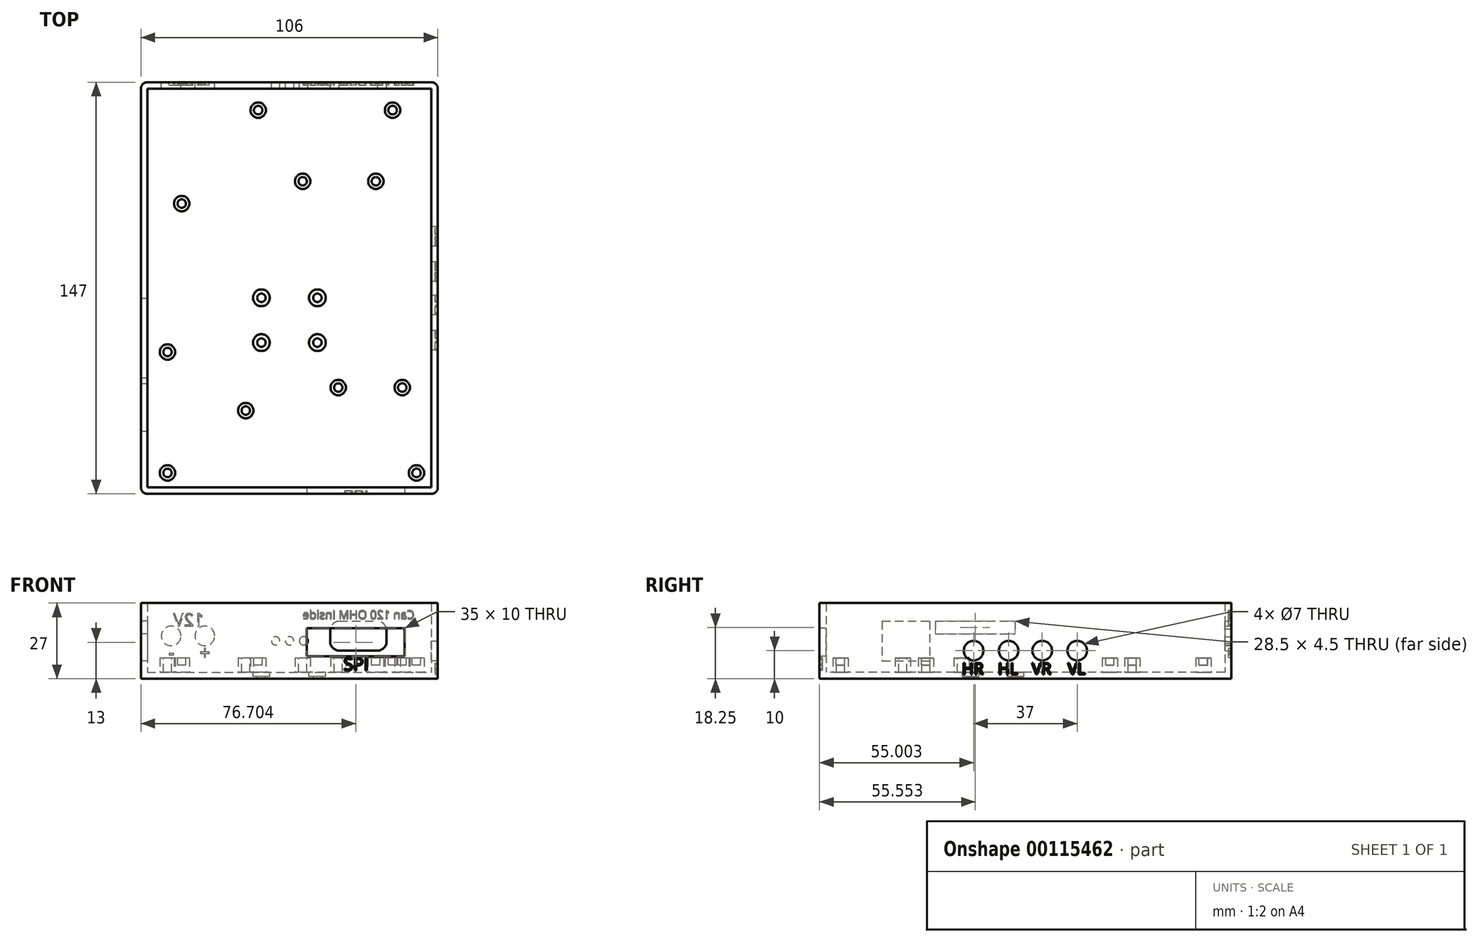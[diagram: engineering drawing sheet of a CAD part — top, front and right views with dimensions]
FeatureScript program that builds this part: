
annotation { "Feature Type Name" : "Feature", "Feature Type Description" : "" }
export const myFeature = defineFeature(function(context is Context, id is Id, definition is map)
    precondition{}
    {
        {
            var Q0;
            Q0=qCreatedBy(makeId("Top.planeOp"),FACE);
            var sketch = newSketch(context, id + "F0", { "sketchPlane" : qUnion([Q0])});
            skLineSegment(sketch, "E0.bottom", {"start": v(-44.59, 115.02) * mm, "end": v(61.41, 115.02) * mm});
            skLineSegment(sketch, "E0.top", {"start": v(-44.59, -31.98) * mm, "end": v(61.41, -31.98) * mm});
            skLineSegment(sketch, "E0.left", {"start": v(-44.59, 115.02) * mm, "end": v(-44.59, -31.98) * mm});
            skLineSegment(sketch, "E0.right", {"start": v(61.41, 115.02) * mm, "end": v(61.41, -31.98) * mm});
            skSolve(sketch);
        }
        {
            var Q0;
            Q0 = qSketchRegion(id + "F0", true);
            extrude(context, id + "F1", {"entities" : qUnion([Q0]), "depth" : 27 * mm});
        }
        {
            var Q0;
            Q0=makeQuery(id+"F1.opExtrude","CAP_FACE",FACE,{"disambiguationData":[OSD([sQuery(id+"F0.wireOp",EDGE,"E0.bottom"),sQuery(id+"F0.wireOp",EDGE,"E0.top"),sQuery(id+"F0.wireOp",EDGE,"E0.left"),sQuery(id+"F0.wireOp",EDGE,"E0.right")])],"isStart":false});
            shell(context, id + "F2", {"entities" : qUnion([Q0]), "thickness" : 2.3 * mm});
        }
        {
            var Q0;
            Q0=makeQuery(id+"F1.opExtrude","SWEPT_FACE",FACE,{"disambiguationData":[OSD([sQuery(id+"F0.wireOp",EDGE,"E0.left")])]});
            var sketch = newSketch(context, id + "F3", { "sketchPlane" : qUnion([Q0])});
            skLineSegment(sketch, "E1", {"start": v(-115.02, 27) * mm, "end": v(-115.02, 0) * mm});
            skLineSegment(sketch, "E2", {"start": v(-115.02, 27) * mm, "end": v(-115.02, 13.5) * mm});
            skLineSegment(sketch, "E3", {"start": v(29.68, 11.5) * mm, "end": v(29.68, 27) * mm});
            skPoint(sketch, "E4.orphan", {"position": v(31.98, 13.5) * mm});
            skPoint(sketch, "E5.left.end.orphan", {"position": v(9.68, 20.5) * mm});
            skLineSegment(sketch, "E6.bottom", {"start": v(9.68, 20.5) * mm, "end": v(-7.32, 20.5) * mm});
            skLineSegment(sketch, "E6.top", {"start": v(9.68, 6.3) * mm, "end": v(-7.32, 6.3) * mm});
            skLineSegment(sketch, "E6.left", {"start": v(9.68, 20.5) * mm, "end": v(9.68, 6.3) * mm});
            skLineSegment(sketch, "E6.right", {"start": v(-7.32, 20.5) * mm, "end": v(-7.32, 6.3) * mm});
            skLineSegment(sketch, "E7", {"start": v(-7.32, 20.5) * mm, "end": v(-9.32, 20.5) * mm});
            skLineSegment(sketch, "E8.bottom", {"start": v(-9.32, 20.5) * mm, "end": v(-37.82, 20.5) * mm});
            skLineSegment(sketch, "E8.top", {"start": v(-9.32, 16) * mm, "end": v(-37.82, 16) * mm});
            skLineSegment(sketch, "E8.left", {"start": v(-9.32, 20.5) * mm, "end": v(-9.32, 16) * mm});
            skLineSegment(sketch, "E8.right", {"start": v(-37.82, 20.5) * mm, "end": v(-37.82, 16) * mm});
            skLineSegment(sketch, "E9", {"start": v(-41.52, 27) * mm, "end": v(-41.52, 0) * mm, "construction": true});
            skLineSegment(sketch, "E10", {"start": v(-115.02, 13.5) * mm, "end": v(31.98, 13.5) * mm, "construction": true});
            skSolve(sketch);
        }
        {
            var Q0;
            Q0 = qSketchRegion(id + "F3", true);
            extrude(context, id + "F4", {"entities" : qUnion([Q0]), "operationType" : NewBodyOperationType.REMOVE, "endBound" : BoundingType.UP_TO_NEXT, "oppositeDirection" : true, "depth" : 25 * mm});
        }
        {
            var Q0;
            Q0=makeQuery(id+"F1.opExtrude","SWEPT_EDGE",EDGE,{"disambiguationData":[OSD([sQuery(id+"F0.wireOp",EDGE,"E0.top"),sQuery(id+"F0.wireOp",EDGE,"E0.left")])]});
            var Q1;
            Q1=makeQuery(id+"F1.opExtrude","SWEPT_EDGE",EDGE,{"disambiguationData":[OSD([sQuery(id+"F0.wireOp",EDGE,"E0.top"),sQuery(id+"F0.wireOp",EDGE,"E0.right")])]});
            var Q2;
            Q2=makeQuery(id+"F1.opExtrude","SWEPT_EDGE",EDGE,{"disambiguationData":[OSD([sQuery(id+"F0.wireOp",EDGE,"E0.bottom"),sQuery(id+"F0.wireOp",EDGE,"E0.right")])]});
            var Q3;
            Q3=makeQuery(id+"F1.opExtrude","SWEPT_EDGE",EDGE,{"disambiguationData":[OSD([sQuery(id+"F0.wireOp",EDGE,"E0.bottom"),sQuery(id+"F0.wireOp",EDGE,"E0.left")])]});
            fillet(context, id + "F5", {"entities" : qUnion([Q0, Q1, Q2, Q3]), "radius" : 2.3 * mm, "tangentPropagation" : true, "allowEdgeOverflow" : false});
        }
        {
            var Q0;
            Q0=makeQuery(id+"F1.opExtrude","SWEPT_FACE",FACE,{"disambiguationData":[OSD([sQuery(id+"F0.wireOp",EDGE,"E0.top")])]});
            var sketch = newSketch(context, id + "F6", { "sketchPlane" : qUnion([Q0])});
            skLineSegment(sketch, "E11", {"start": v(-42.29, 8) * mm, "end": v(59.11, 8) * mm, "construction": true});
            skLineSegment(sketch, "E12.top", {"start": v(23.11, 8) * mm, "end": v(58.16, 8) * mm});
            skPoint(sketch, "E13.end.orphan", {"position": v(12.91, 8) * mm});
            skLineSegment(sketch, "E14", {"start": v(12.91, 8) * mm, "end": v(38.58, 8) * mm});
            skLineSegment(sketch, "E15.bottom", {"start": v(14.61, 8) * mm, "end": v(49.61, 8) * mm});
            skLineSegment(sketch, "E15.top", {"start": v(14.61, 18) * mm, "end": v(49.61, 18) * mm});
            skLineSegment(sketch, "E15.left", {"start": v(14.61, 8) * mm, "end": v(14.61, 18) * mm});
            skLineSegment(sketch, "E15.right", {"start": v(49.61, 8) * mm, "end": v(49.61, 18) * mm});
            skLineSegment(sketch, "E16", {"start": v(8.41, 27) * mm, "end": v(8.41, 0) * mm, "construction": true});
            skLineSegment(sketch, "E17", {"start": v(-42.29, 13.5) * mm, "end": v(59.11, 13.5) * mm, "construction": true});
            skSolve(sketch);
        }
        {
            var Q0;
            Q0 = qSketchRegion(id + "F6", true);
            extrude(context, id + "F7", {"entities" : qUnion([Q0]), "operationType" : NewBodyOperationType.REMOVE, "endBound" : BoundingType.UP_TO_NEXT, "oppositeDirection" : true, "depth" : 25 * mm});
        }
        {
            var Q0;
            Q0=makeQuery(id+"F1.opExtrude","SWEPT_FACE",FACE,{"disambiguationData":[OSD([sQuery(id+"F0.wireOp",EDGE,"E0.right")])]});
            var sketch = newSketch(context, id + "F8", { "sketchPlane" : qUnion([Q0])});
            skLineSegment(sketch, "E18", {"start": v(19.52, 10) * mm, "end": v(26.52, 10) * mm});
            skCircle(sketch, "E19", {"center": v(23.02, 10) * mm, "radius": 3.5 * mm});
            skCircle(sketch, "E20", {"center": v(35.52, 10) * mm, "radius": 3.5 * mm});
            skCircle(sketch, "E21", {"center": v(47.52, 10) * mm, "radius": 3.5 * mm});
            skCircle(sketch, "E22", {"center": v(60.02, 10) * mm, "radius": 3.5 * mm});
            skLineSegment(sketch, "E23.trimOffspring", {"start": v(32.02, 10) * mm, "end": v(39.02, 10) * mm});
            skLineSegment(sketch, "E24.trimOffspring", {"start": v(44.02, 10) * mm, "end": v(51.02, 10) * mm});
            skPoint(sketch, "E25.orphan", {"position": v(41.52, 27) * mm});
            skLineSegment(sketch, "E26.trimOffspring", {"start": v(56.52, 10) * mm, "end": v(63.52, 10) * mm});
            skLineSegment(sketch, "E27", {"start": v(41.52, 27) * mm, "end": v(41.52, 0) * mm});
            skLineSegment(sketch, "E28", {"start": v(35.52, 10) * mm, "end": v(-29.68, 10) * mm});
            skLineSegment(sketch, "E29", {"start": v(-29.68, 10) * mm, "end": v(112.72, 10) * mm});
            skSolve(sketch);
        }
        {
            var Q0;
            Q0 = qSketchRegion(id + "F8", true);
            extrude(context, id + "F9", {"entities" : qUnion([Q0]), "operationType" : NewBodyOperationType.REMOVE, "endBound" : BoundingType.UP_TO_NEXT, "oppositeDirection" : true, "depth" : 25 * mm});
        }
        {
            var Q0;
            Q0=makeQuery(id+"F1.opExtrude","SWEPT_FACE",FACE,{"disambiguationData":[OSD([sQuery(id+"F0.wireOp",EDGE,"E0.bottom")])]});
            var sketch = newSketch(context, id + "F10", { "sketchPlane" : qUnion([Q0])});
            skLineSegment(sketch, "E30", {"start": v(-39.9, 10) * mm, "end": v(-26.2, 10) * mm});
            skLineSegment(sketch, "E31", {"start": v(-26.2, 20.5) * mm, "end": v(-39.9, 20.5) * mm});
            skArc(sketch, "E32.trimOffspring", {"start": v(-22.97, 17.81) * mm, "mid": v(-24.12, 19.72) * mm, "end": v(-26.2, 20.5) * mm});
            skArc(sketch, "E33.trimOffspring", {"start": v(-26.2, 10) * mm, "mid": v(-24.13, 10.8) * mm, "end": v(-23, 12.71) * mm});
            skArc(sketch, "E34.trimOffspring", {"start": v(-43.12, 12.7) * mm, "mid": v(-41.98, 10.8) * mm, "end": v(-39.9, 10) * mm});
            skLineSegment(sketch, "E35", {"start": v(-43.12, 12.7) * mm, "end": v(-43.12, 17.8) * mm});
            skPoint(sketch, "E36.center.orphan", {"position": v(-40.53, 15.25) * mm});
            skCircle(sketch, "E37", {"center": v(21.79, 15.25) * mm, "radius": 3.5 * mm});
            skCircle(sketch, "E38", {"center": v(33.79, 15.25) * mm, "radius": 3.5 * mm});
            skPoint(sketch, "E39", {"position": v(42.29, 13.5) * mm});
            skPoint(sketch, "E40.start.orphan", {"position": v(-59.11, 7) * mm});
            skLineSegment(sketch, "E41", {"start": v(-22.97, 17.81) * mm, "end": v(-23, 12.71) * mm});
            skArc(sketch, "E42.trimOffspring", {"start": v(-39.9, 20.5) * mm, "mid": v(-41.97, 19.7) * mm, "end": v(-43.12, 17.8) * mm});
            skPoint(sketch, "E43.center.orphan", {"position": v(-39.9, 12.3) * mm});
            skPoint(sketch, "E44.center.orphan", {"position": v(-39.9, 8.6) * mm});
            skPoint(sketch, "E45.orphan", {"position": v(42.29, 20.72) * mm});
            skPoint(sketch, "E46.start.orphan", {"position": v(-59.11, 20.72) * mm});
            skLineSegment(sketch, "E47", {"start": v(-59.11, 13.5) * mm, "end": v(42.29, 13.5) * mm, "construction": true});
            skCircle(sketch, "E48", {"center": v(-13.5, 13.5) * mm, "radius": 1.5 * mm});
            skCircle(sketch, "E49", {"center": v(-8.5, 13.5) * mm, "radius": 1.5 * mm});
            skCircle(sketch, "E50", {"center": v(-3.5, 13.5) * mm, "radius": 1.5 * mm});
            skLineSegment(sketch, "E51", {"start": v(-8.41, 27) * mm, "end": v(-8.41, 0) * mm, "construction": true});
            skLineSegment(sketch, "E52", {"start": v(-43.12, 15.25) * mm, "end": v(-22.98, 15.3) * mm, "construction": true});
            skLineSegment(sketch, "E53", {"start": v(-33.05, 20.5) * mm, "end": v(-33.02, 10) * mm, "construction": true});
            skSolve(sketch);
        }
        {
            var Q0;
            Q0 = qSketchRegion(id + "F10", true);
            extrude(context, id + "F11", {"entities" : qUnion([Q0]), "operationType" : NewBodyOperationType.REMOVE, "endBound" : BoundingType.UP_TO_NEXT, "oppositeDirection" : true, "depth" : 25 * mm});
        }
        {
            var Q0;
            Q0=makeQuery(id+"F1.opExtrude","SWEPT_FACE",FACE,{"disambiguationData":[OSD([sQuery(id+"F0.wireOp",EDGE,"E0.right")])]});
            var sketch = newSketch(context, id + "F12", { "sketchPlane" : qUnion([Q0])});
            skText(sketch, "E54", { "text": "HR", "fontName": "OpenSans-Regular.ttf"});
            skText(sketch, "E55", { "text": "HL", "fontName": "OpenSans-Regular.ttf"});
            skText(sketch, "E56", { "text": "VR", "fontName": "OpenSans-Regular.ttf"});
            skText(sketch, "E57", { "text": "VL", "fontName": "OpenSans-Regular.ttf"});
            skLineSegment(sketch, "E58", {"start": v(22.84, 5.63) * mm, "end": v(22.84, 9.12) * mm, "construction": true});
            const initialGuessF12  = {"E54": [0.01884, 0.00153, 1, 0, 0.0041], "E55": [0.03172, 0.00153, 1, 0, 0.0041], "E56": [0.04382, 0.00153, 1, 0, 0.0041], "E57": [0.05666, 0.00153, 1, 0, 0.0041]};
            skSetInitialGuess(sketch, initialGuessF12);
            skSolve(sketch);
        }
        {
            var Q0;
            Q0 = qSketchRegion(id + "F12", true);
            extrude(context, id + "F13", {"entities" : qUnion([Q0]), "operationType" : NewBodyOperationType.REMOVE, "oppositeDirection" : true, "depth" : 1 * mm});
        }
        {
            var Q0;
            Q0=makeQuery(id+"F1.opExtrude","SWEPT_FACE",FACE,{"disambiguationData":[OSD([sQuery(id+"F0.wireOp",EDGE,"E0.top")])]});
            var sketch = newSketch(context, id + "F14", { "sketchPlane" : qUnion([Q0])});
            skText(sketch, "E59", { "text": "SPI", "fontName": "OpenSans-Regular.ttf"});
            skPoint(sketch, "E60", {"position": v(32.11, 8) * mm});
            skLineSegment(sketch, "E61", {"start": v(32.11, 7.44) * mm, "end": v(32.11, 10.56) * mm, "construction": true});
            const initialGuessF14  = {"E59": [0.02775, 0.00294, 1, 0, 0.0045]};
            skSetInitialGuess(sketch, initialGuessF14);
            skSolve(sketch);
        }
        {
            var Q0;
            Q0 = qSketchRegion(id + "F14", true);
            extrude(context, id + "F15", {"entities" : qUnion([Q0]), "operationType" : NewBodyOperationType.REMOVE, "oppositeDirection" : true, "depth" : 1 * mm});
        }
        {
            var Q0;
            Q0=makeQuery(id+"F1.opExtrude","SWEPT_FACE",FACE,{"disambiguationData":[OSD([sQuery(id+"F0.wireOp",EDGE,"E0.bottom")])]});
            var sketch = newSketch(context, id + "F16", { "sketchPlane" : qUnion([Q0])});
            skText(sketch, "E62", { "text": "Can 120 OHM Inside", "fontName": "OpenSans-Regular.ttf"});
            skText(sketch, "E63", { "text": "+", "fontName": "OpenSans-Regular.ttf"});
            skText(sketch, "E64", { "text": "-", "fontName": "OpenSans-Regular.ttf"});
            skText(sketch, "E65", { "text": "12V", "fontName": "OpenSans-Regular.ttf"});
            skPoint(sketch, "E66", {"position": v(-33.05, 20.5) * mm});
            skLineSegment(sketch, "E67", {"start": v(-33.05, 24.32) * mm, "end": v(-33.05, 16.73) * mm, "construction": true});
            const initialGuessF16  = {"E62": [-0.05305, 0.0213, 1, 0, 0.00302], "E63": [0.01979, 0.00683, 1, 0, 0.00492], "E64": [0.03263, 0.00695, 1, 0, 0.0048], "E65": [0.02215, 0.01873, 1, 0, 0.0045]};
            skSetInitialGuess(sketch, initialGuessF16);
            skSolve(sketch);
        }
        {
            var Q0;
            Q0 = qSketchRegion(id + "F16", true);
            extrude(context, id + "F17", {"entities" : qUnion([Q0]), "operationType" : NewBodyOperationType.REMOVE, "oppositeDirection" : true, "depth" : 1 * mm});
        }
        {
            var Q0;
            Q0 = qSketchRegion(id + "F16", true);
            extrude(context, id + "F18", {"entities" : qUnion([Q0]), "operationType" : NewBodyOperationType.REMOVE, "oppositeDirection" : true, "depth" : 1 * mm});
        }
        {
            var Q0;
            Q0=makeQuery(id+"F2.opShell","OFFSET_FACE",FACE,{"disambiguationData":[OSD([sQuery(id+"F0.wireOp",EDGE,"E0.bottom"),sQuery(id+"F0.wireOp",EDGE,"E0.top"),sQuery(id+"F0.wireOp",EDGE,"E0.left"),sQuery(id+"F0.wireOp",EDGE,"E0.right")])]});
            var sketch = newSketch(context, id + "F19", { "sketchPlane" : qUnion([Q0])});
            skPoint(sketch, "E68.trimOffspring.end.orphan", {"position": v(59.11, -22.18) * mm});
            skPoint(sketch, "E69.start.orphan", {"position": v(-42.29, -22.18) * mm});
            skPoint(sketch, "E70.orphan", {"position": v(60.61, 112.72) * mm});
            skPoint(sketch, "E71.orphan", {"position": v(59.11, 103.22) * mm});
            skPoint(sketch, "E72.center.orphan", {"position": v(-43.79, -22.18) * mm});
            skSolve(sketch);
        }
        {
            var Q0;
            Q0=makeQuery(id+"F2.opShell","OFFSET_FACE",FACE,{"disambiguationData":[OSD([sQuery(id+"F0.wireOp",EDGE,"E0.bottom"),sQuery(id+"F0.wireOp",EDGE,"E0.top"),sQuery(id+"F0.wireOp",EDGE,"E0.left"),sQuery(id+"F0.wireOp",EDGE,"E0.right")])]});
            var sketch = newSketch(context, id + "F20", { "sketchPlane" : qUnion([Q0])});
            skCircle(sketch, "E73", {"center": v(-1.59, 38.02) * mm, "radius": 3 * mm});
            skCircle(sketch, "E74", {"center": v(18.41, 38.02) * mm, "radius": 3 * mm});
            skCircle(sketch, "E75", {"center": v(-1.59, 22.02) * mm, "radius": 3 * mm});
            skCircle(sketch, "E76", {"center": v(18.41, 22.02) * mm, "radius": 3 * mm});
            skCircle(sketch, "E77", {"center": v(-1.59, 22.02) * mm, "radius": 1.5 * mm});
            skCircle(sketch, "E78", {"center": v(-1.59, 38.02) * mm, "radius": 1.5 * mm});
            skCircle(sketch, "E79", {"center": v(18.41, 38.02) * mm, "radius": 1.5 * mm});
            skCircle(sketch, "E80", {"center": v(18.41, 22.02) * mm, "radius": 1.5 * mm});
            skLineSegment(sketch, "E81", {"start": v(-1.59, 38.02) * mm, "end": v(18.41, 38.02) * mm});
            skLineSegment(sketch, "E82", {"start": v(18.41, 22.02) * mm, "end": v(-1.59, 22.02) * mm, "construction": true});
            skLineSegment(sketch, "E83", {"start": v(-1.59, 38.02) * mm, "end": v(18.41, 38.02) * mm, "construction": true});
            skLineSegment(sketch, "E84", {"start": v(18.41, 22.02) * mm, "end": v(18.41, 38.02) * mm, "construction": true});
            skLineSegment(sketch, "E85", {"start": v(-1.59, 22.02) * mm, "end": v(-1.59, 38.02) * mm, "construction": true});
            skLineSegment(sketch, "E86", {"start": v(59.11, 41.52) * mm, "end": v(-42.29, 41.52) * mm, "construction": true});
            skLineSegment(sketch, "E87", {"start": v(8.41, 112.72) * mm, "end": v(8.41, -29.68) * mm, "construction": true});
            skLineSegment(sketch, "E88.bottom", {"start": v(35.11, 15.02) * mm, "end": v(-18.29, 15.02) * mm, "construction": true});
            skLineSegment(sketch, "E88.top", {"start": v(35.11, 45.02) * mm, "end": v(-18.29, 45.02) * mm, "construction": true});
            skLineSegment(sketch, "E88.left", {"start": v(35.11, 15.02) * mm, "end": v(35.11, 45.02) * mm, "construction": true});
            skLineSegment(sketch, "E88.right", {"start": v(-18.29, 15.02) * mm, "end": v(-18.29, 45.02) * mm, "construction": true});
            skSolve(sketch);
        }
        {
            var Q0;
            Q0 = qSketchRegion(id + "F20", true);
            extrude(context, id + "F21", {"entities" : qUnion([Q0]), "operationType" : NewBodyOperationType.REMOVE, "oppositeDirection" : true, "depth" : 1.5 * mm});
        }
        {
            var Q0;
            Q0=makeQuery(id+"F21.boolean.opBoolean","SPLIT",FACE,{"disambiguationData":[TD([makeQuery(id+"F21.opExtrude","SWEPT_FACE",FACE,{"disambiguationData":[OSD([sQuery(id+"F20.wireOp",EDGE,"E80")])]})])],"derivedFrom":makeQuery(id+"F2.opShell","OFFSET_FACE",FACE,{"disambiguationData":[OSD([sQuery(id+"F0.wireOp",EDGE,"E0.bottom"),sQuery(id+"F0.wireOp",EDGE,"E0.top"),sQuery(id+"F0.wireOp",EDGE,"E0.left"),sQuery(id+"F0.wireOp",EDGE,"E0.right")])]})});
            var Q1;
            Q1=makeQuery(id+"F21.boolean.opBoolean","SPLIT",FACE,{"disambiguationData":[TD([makeQuery(id+"F21.opExtrude","SWEPT_FACE",FACE,{"disambiguationData":[OSD([sQuery(id+"F20.wireOp",EDGE,"E77")])]})])],"derivedFrom":makeQuery(id+"F2.opShell","OFFSET_FACE",FACE,{"disambiguationData":[OSD([sQuery(id+"F0.wireOp",EDGE,"E0.bottom"),sQuery(id+"F0.wireOp",EDGE,"E0.top"),sQuery(id+"F0.wireOp",EDGE,"E0.left"),sQuery(id+"F0.wireOp",EDGE,"E0.right")])]})});
            var Q2;
            Q2=makeQuery(id+"F21.boolean.opBoolean","SPLIT",FACE,{"disambiguationData":[TD([makeQuery(id+"F21.opExtrude","SWEPT_FACE",FACE,{"disambiguationData":[OSD([sQuery(id+"F20.wireOp",EDGE,"E78")])]})])],"derivedFrom":makeQuery(id+"F2.opShell","OFFSET_FACE",FACE,{"disambiguationData":[OSD([sQuery(id+"F0.wireOp",EDGE,"E0.bottom"),sQuery(id+"F0.wireOp",EDGE,"E0.top"),sQuery(id+"F0.wireOp",EDGE,"E0.left"),sQuery(id+"F0.wireOp",EDGE,"E0.right")])]})});
            var Q3;
            Q3=makeQuery(id+"F21.boolean.opBoolean","SPLIT",FACE,{"disambiguationData":[TD([makeQuery(id+"F21.opExtrude","SWEPT_FACE",FACE,{"disambiguationData":[OSD([sQuery(id+"F20.wireOp",EDGE,"E79")])]})])],"derivedFrom":makeQuery(id+"F2.opShell","OFFSET_FACE",FACE,{"disambiguationData":[OSD([sQuery(id+"F0.wireOp",EDGE,"E0.bottom"),sQuery(id+"F0.wireOp",EDGE,"E0.top"),sQuery(id+"F0.wireOp",EDGE,"E0.left"),sQuery(id+"F0.wireOp",EDGE,"E0.right")])]})});
            var Q4;
            Q4=sQuery(id+"F20.wireOp",EDGE,"E80");
            var Q5;
            Q5=sQuery(id+"F20.wireOp",EDGE,"E77");
            var Q6;
            Q6=sQuery(id+"F20.wireOp",EDGE,"E78");
            var Q7;
            Q7=sQuery(id+"F20.wireOp",EDGE,"E79");
            extrude(context, id + "F22", {"entities" : qUnion([Q0, Q1, Q2, Q3]), "operationType" : NewBodyOperationType.REMOVE, "surfaceEntities" : qUnion([Q4, Q5, Q6, Q7]), "endBound" : BoundingType.UP_TO_NEXT, "oppositeDirection" : true, "depth" : 25 * mm});
        }
        {
            var Q0;
            {var subQ30=sQuery(id+"F0.wireOp",EDGE,"E0.bottom");Q0=makeQuery(id+"F19.imprint","IMPRINT",FACE,{"disambiguationData":[TD([[makeQuery(id+"F19.imprint","IMPRINT",EDGE,{"derivedFrom":makeQuery(id+"F2.opShell","OFFSET_EDGE",EDGE,{"disambiguationData":[OSD([subQ30]),TDD([makeQuery(id+"F1.opExtrude","CAP_EDGE",EDGE,{"disambiguationData":[OSD([subQ30])],"isStart":true})])]})}),-1.0]])]});}
            var sketch = newSketch(context, id + "F23", { "sketchPlane" : qUnion([Q0])});
            skCircle(sketch, "E89", {"center": v(53.8, -24.5) * mm, "radius": 2.75 * mm});
            skCircle(sketch, "E90", {"center": v(-2.72, 105.04) * mm, "radius": 2.75 * mm});
            skCircle(sketch, "E91", {"center": v(45.25, 105.04) * mm, "radius": 2.75 * mm});
            skCircle(sketch, "E92", {"center": v(48.71, 5.98) * mm, "radius": 2.75 * mm});
            skCircle(sketch, "E93", {"center": v(-30.03, 71.67) * mm, "radius": 2.75 * mm});
            skCircle(sketch, "E94", {"center": v(39.27, 79.64) * mm, "radius": 2.75 * mm});
            skCircle(sketch, "E95", {"center": v(-7.17, -2.24) * mm, "radius": 2.75 * mm});
            skCircle(sketch, "E96", {"center": v(25.85, 5.98) * mm, "radius": 2.75 * mm});
            skCircle(sketch, "E97", {"center": v(13.15, 79.64) * mm, "radius": 2.75 * mm});
            skPoint(sketch, "E98.orphan", {"position": v(-42.3, 41.52) * mm});
            skCircle(sketch, "E99", {"center": v(-35.1, 18.68) * mm, "radius": 2.75 * mm});
            skCircle(sketch, "E100", {"center": v(-35.1, -24.5) * mm, "radius": 2.75 * mm});
            skLineSegment(sketch, "E101.trimOffspring", {"start": v(51.09, -24) * mm, "end": v(53.8, -24.5) * mm, "construction": true});
            skPoint(sketch, "E102.start.orphan", {"position": v(67.97, 41.52) * mm});
            skLineSegment(sketch, "E103", {"start": v(-42.3, 41.52) * mm, "end": v(59.13, 41.52) * mm, "construction": true});
            skLineSegment(sketch, "E104", {"start": v(8.41, 41.52) * mm, "end": v(8.41, -29.9) * mm, "construction": true});
            skLineSegment(sketch, "E105", {"start": v(8.41, -29.9) * mm, "end": v(8.41, 112.24) * mm, "construction": true});
            skSolve(sketch);
        }
        {
            var Q0;
            Q0 = qSketchRegion(id + "F23", true);
            extrude(context, id + "F24", {"entities" : qUnion([Q0]), "operationType" : NewBodyOperationType.ADD, "depth" : 5 * mm});
        }
        {
            var Q0;
            Q0=makeQuery(id+"F24.opExtrude","CAP_FACE",FACE,{"disambiguationData":[OSD([sQuery(id+"F23.wireOp",EDGE,"E90")])],"isStart":false});
            var sketch = newSketch(context, id + "F25", { "sketchPlane" : qUnion([Q0])});
            skCircle(sketch, "E106", {"center": v(-2.72, 105.04) * mm, "radius": 1.53 * mm});
            skSolve(sketch);
        }
        {
            var Q0;
            Q0 = qSketchRegion(id + "F25", true);
            extrude(context, id + "F26", {"entities" : qUnion([Q0]), "operationType" : NewBodyOperationType.REMOVE, "oppositeDirection" : true, "depth" : 5 * mm, "symmetric" : true});
        }
        {
            var Q0;
            Q0=makeQuery(id+"F24.opExtrude","CAP_FACE",FACE,{"disambiguationData":[OSD([sQuery(id+"F23.wireOp",EDGE,"E91")])],"isStart":false});
            var sketch = newSketch(context, id + "F27", { "sketchPlane" : qUnion([Q0])});
            skCircle(sketch, "E107", {"center": v(45.25, 105.04) * mm, "radius": 1.54 * mm});
            skSolve(sketch);
        }
        {
            var Q0;
            Q0 = qSketchRegion(id + "F27", true);
            extrude(context, id + "F28", {"entities" : qUnion([Q0]), "operationType" : NewBodyOperationType.REMOVE, "oppositeDirection" : true, "depth" : 5 * mm, "symmetric" : true});
        }
        {
            var Q0;
            Q0=makeQuery(id+"F24.opExtrude","CAP_FACE",FACE,{"disambiguationData":[OSD([sQuery(id+"F23.wireOp",EDGE,"E89")])],"isStart":false});
            var sketch = newSketch(context, id + "F29", { "sketchPlane" : qUnion([Q0])});
            skCircle(sketch, "E108", {"center": v(53.8, -24.5) * mm, "radius": 1.53 * mm});
            skSolve(sketch);
        }
        {
            var Q0;
            Q0 = qSketchRegion(id + "F29", true);
            extrude(context, id + "F30", {"entities" : qUnion([Q0]), "operationType" : NewBodyOperationType.REMOVE, "oppositeDirection" : true, "depth" : 5 * mm, "symmetric" : true});
        }
        {
            var Q0;
            Q0=makeQuery(id+"F24.opExtrude","CAP_FACE",FACE,{"disambiguationData":[OSD([sQuery(id+"F23.wireOp",EDGE,"E92")])],"isStart":false});
            var sketch = newSketch(context, id + "F31", { "sketchPlane" : qUnion([Q0])});
            skCircle(sketch, "E109", {"center": v(48.71, 5.98) * mm, "radius": 1.52 * mm});
            skSolve(sketch);
        }
        {
            var Q0;
            Q0 = qSketchRegion(id + "F31", true);
            extrude(context, id + "F32", {"entities" : qUnion([Q0]), "operationType" : NewBodyOperationType.REMOVE, "oppositeDirection" : true, "depth" : 5 * mm, "symmetric" : true});
        }
        {
            var Q0;
            Q0=makeQuery(id+"F24.opExtrude","CAP_FACE",FACE,{"disambiguationData":[OSD([sQuery(id+"F23.wireOp",EDGE,"E94")])],"isStart":false});
            var sketch = newSketch(context, id + "F33", { "sketchPlane" : qUnion([Q0])});
            skCircle(sketch, "E110", {"center": v(39.27, 79.64) * mm, "radius": 1.5 * mm});
            skSolve(sketch);
        }
        {
            var Q0;
            Q0 = qSketchRegion(id + "F33", true);
            extrude(context, id + "F34", {"entities" : qUnion([Q0]), "operationType" : NewBodyOperationType.REMOVE, "oppositeDirection" : true, "depth" : 5 * mm, "symmetric" : true});
        }
        {
            var Q0;
            Q0=makeQuery(id+"F24.opExtrude","CAP_FACE",FACE,{"disambiguationData":[OSD([sQuery(id+"F23.wireOp",EDGE,"E93")])],"isStart":false});
            var sketch = newSketch(context, id + "F35", { "sketchPlane" : qUnion([Q0])});
            skCircle(sketch, "E111", {"center": v(-30.03, 71.67) * mm, "radius": 1.5 * mm});
            skSolve(sketch);
        }
        {
            var Q0;
            Q0 = qSketchRegion(id + "F35", true);
            extrude(context, id + "F36", {"entities" : qUnion([Q0]), "operationType" : NewBodyOperationType.REMOVE, "oppositeDirection" : true, "depth" : 5 * mm, "symmetric" : true});
        }
        {
            var Q0;
            Q0=makeQuery(id+"F24.opExtrude","CAP_FACE",FACE,{"disambiguationData":[OSD([sQuery(id+"F23.wireOp",EDGE,"E95")])],"isStart":false});
            var sketch = newSketch(context, id + "F37", { "sketchPlane" : qUnion([Q0])});
            skCircle(sketch, "E112", {"center": v(-7.17, -2.24) * mm, "radius": 1.5 * mm});
            skSolve(sketch);
        }
        {
            var Q0;
            Q0 = qSketchRegion(id + "F37", true);
            extrude(context, id + "F38", {"entities" : qUnion([Q0]), "operationType" : NewBodyOperationType.REMOVE, "oppositeDirection" : true, "depth" : 5 * mm});
        }
        {
            var Q0;
            Q0=makeQuery(id+"F24.opExtrude","CAP_FACE",FACE,{"disambiguationData":[OSD([sQuery(id+"F23.wireOp",EDGE,"E96")])],"isStart":false});
            var sketch = newSketch(context, id + "F39", { "sketchPlane" : qUnion([Q0])});
            skCircle(sketch, "E113", {"center": v(25.85, 5.98) * mm, "radius": 1.5 * mm});
            skSolve(sketch);
        }
        {
            var Q0;
            Q0 = qSketchRegion(id + "F39", true);
            extrude(context, id + "F40", {"entities" : qUnion([Q0]), "operationType" : NewBodyOperationType.REMOVE, "oppositeDirection" : true, "depth" : 5 * mm});
        }
        {
            var Q0;
            Q0=makeQuery(id+"F24.opExtrude","CAP_FACE",FACE,{"disambiguationData":[OSD([sQuery(id+"F23.wireOp",EDGE,"E97")])],"isStart":false});
            var sketch = newSketch(context, id + "F41", { "sketchPlane" : qUnion([Q0])});
            skCircle(sketch, "E114", {"center": v(13.15, 79.64) * mm, "radius": 1.5 * mm});
            skSolve(sketch);
        }
        {
            var Q0;
            Q0 = qSketchRegion(id + "F41", true);
            extrude(context, id + "F42", {"entities" : qUnion([Q0]), "operationType" : NewBodyOperationType.REMOVE, "oppositeDirection" : true, "depth" : 5 * mm});
        }
        {
            var Q0;
            Q0=makeQuery(id+"F24.opExtrude","CAP_FACE",FACE,{"disambiguationData":[OSD([sQuery(id+"F23.wireOp",EDGE,"E99")])],"isStart":false});
            var sketch = newSketch(context, id + "F43", { "sketchPlane" : qUnion([Q0])});
            skCircle(sketch, "E115", {"center": v(-35.1, 18.68) * mm, "radius": 1.5 * mm});
            skSolve(sketch);
        }
        {
            var Q0;
            Q0 = qSketchRegion(id + "F43", true);
            extrude(context, id + "F44", {"entities" : qUnion([Q0]), "operationType" : NewBodyOperationType.REMOVE, "oppositeDirection" : true, "depth" : 5 * mm});
        }
        {
            var Q0;
            Q0=makeQuery(id+"F24.opExtrude","CAP_FACE",FACE,{"disambiguationData":[OSD([sQuery(id+"F23.wireOp",EDGE,"E100")])],"isStart":false});
            var sketch = newSketch(context, id + "F45", { "sketchPlane" : qUnion([Q0])});
            skCircle(sketch, "E116", {"center": v(-35.1, -24.5) * mm, "radius": 1.5 * mm});
            skSolve(sketch);
        }
        {
            var Q0;
            Q0 = qSketchRegion(id + "F45", true);
            extrude(context, id + "F46", {"entities" : qUnion([Q0]), "operationType" : NewBodyOperationType.REMOVE, "oppositeDirection" : true, "depth" : 5 * mm});
        }
    });
